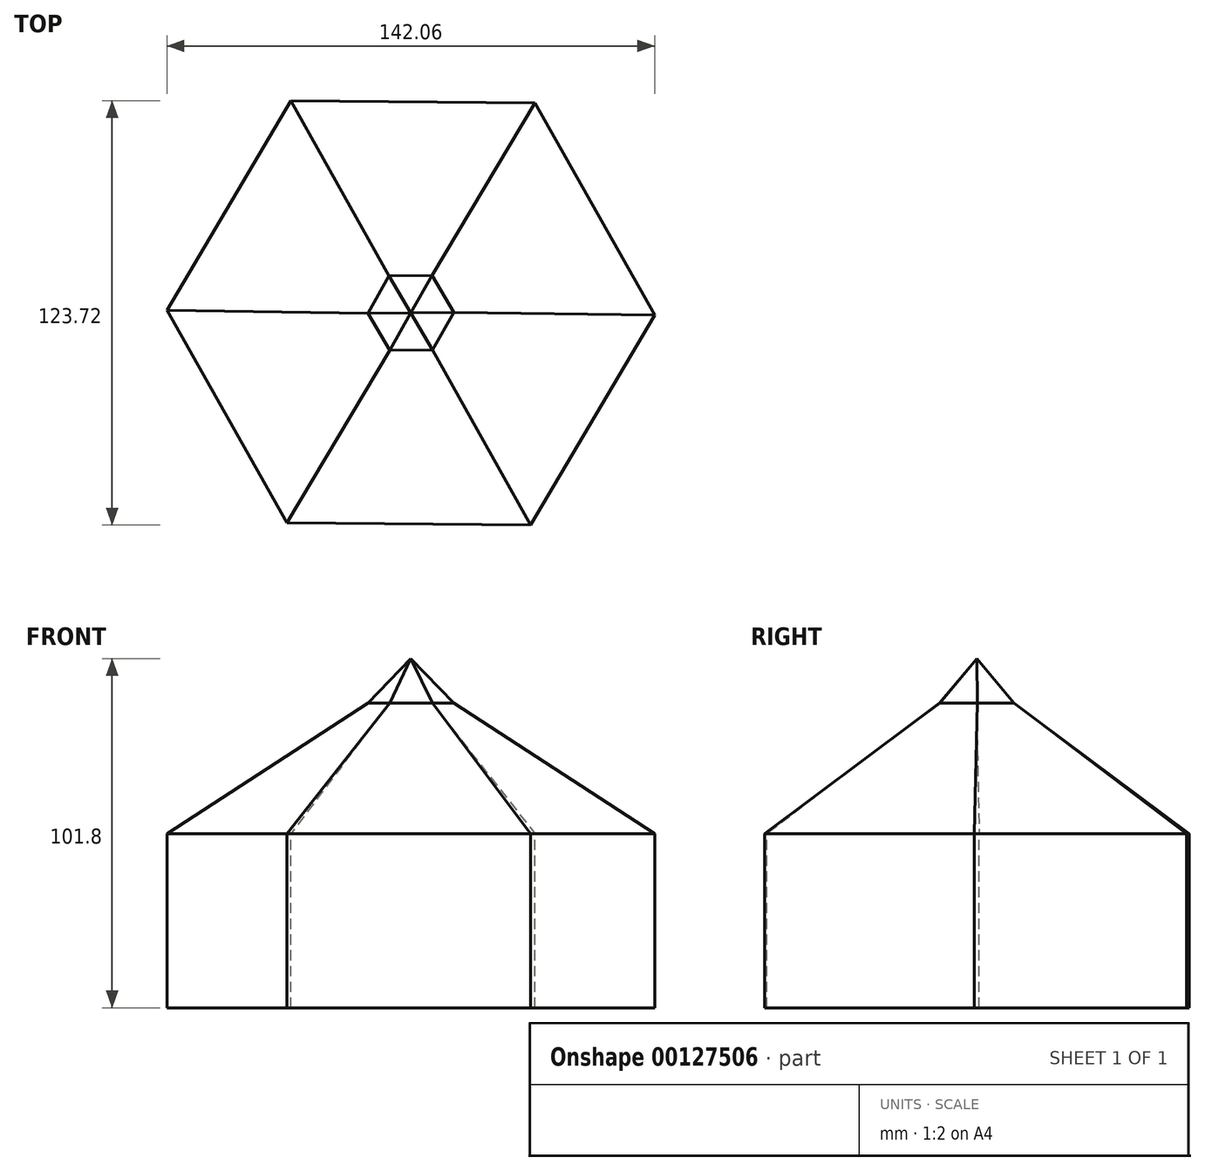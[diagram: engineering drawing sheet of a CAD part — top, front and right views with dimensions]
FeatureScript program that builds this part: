
annotation { "Feature Type Name" : "Feature", "Feature Type Description" : "" }
export const myFeature = defineFeature(function(context is Context, id is Id, definition is map)
    precondition{}
    {
        {
            var Q0;
            Q0=qCreatedBy(makeId("Top.planeOp"),FACE);
            cPlane(context, id + "F0", {"entities" : qUnion([Q0]), "cplaneType" : CPlaneType.OFFSET, "offset" : 38.1 * mm, "width" : 152.4 * mm, "height" : 152.4 * mm});
        }
        {
            var Q0;
            Q0=qCreatedBy(makeId("Top.planeOp"),FACE);
            var sketch = newSketch(context, id + "F1", { "sketchPlane" : qUnion([Q0])});
            skCircle(sketch, "E0.cCircle", {"center": v(0, 0) * mm, "radius": 61.51 * mm, "construction": true});
            skLineSegment(sketch, "E0.0", {"start": v(36.1, 61.17) * mm, "end": v(71.03, -0.69) * mm});
            skLineSegment(sketch, "E0.1", {"start": v(71.03, -0.69) * mm, "end": v(34.92, -61.86) * mm});
            skLineSegment(sketch, "E0.2", {"start": v(34.92, -61.86) * mm, "end": v(-36.1, -61.17) * mm});
            skLineSegment(sketch, "E0.3", {"start": v(-36.1, -61.17) * mm, "end": v(-71.03, 0.69) * mm});
            skLineSegment(sketch, "E0.4", {"start": v(-71.03, 0.69) * mm, "end": v(-34.92, 61.86) * mm});
            skLineSegment(sketch, "E0.5", {"start": v(-34.92, 61.86) * mm, "end": v(36.1, 61.17) * mm});
            skPoint(sketch, "E0.0.midPoint", {"position": v(53.57, 30.24) * mm});
            skSolve(sketch);
        }
        {
            var Q0;
            Q0 = qSketchRegion(id + "F1", true);
            extrude(context, id + "F2", {"entities" : qUnion([Q0]), "oppositeDirection" : true, "depth" : 50.8 * mm});
        }
        {
            var Q0;
            Q0=qCreatedBy(id+"F0.planeOp",FACE);
            var sketch = newSketch(context, id + "F3", { "sketchPlane" : qUnion([Q0])});
            skCircle(sketch, "E1.cCircle", {"center": v(0, 0) * mm, "radius": 10.83 * mm, "construction": true});
            skLineSegment(sketch, "E1.0", {"start": v(12.5, 0.11) * mm, "end": v(6.35, -10.77) * mm});
            skLineSegment(sketch, "E1.1", {"start": v(6.35, -10.77) * mm, "end": v(-6.15, -10.88) * mm});
            skLineSegment(sketch, "E1.2", {"start": v(-6.15, -10.88) * mm, "end": v(-12.5, -0.11) * mm});
            skLineSegment(sketch, "E1.3", {"start": v(-12.5, -0.11) * mm, "end": v(-6.35, 10.77) * mm});
            skLineSegment(sketch, "E1.4", {"start": v(-6.35, 10.77) * mm, "end": v(6.15, 10.88) * mm});
            skLineSegment(sketch, "E1.5", {"start": v(6.15, 10.88) * mm, "end": v(12.5, 0.11) * mm});
            skPoint(sketch, "E1.0.midPoint", {"position": v(9.42, -5.33) * mm});
            skSolve(sketch);
        }
        {
            var Q1;
            Q1=makeQuery(id+"F3.imprint","IMPRINT",FACE,{"disambiguationData":[TD([[makeQuery(id+"F3.imprint","IMPRINT",EDGE,{"derivedFrom":sQuery(id+"F3.wireOp",EDGE,"E1.0")}),-1.0]])]});
            var Q2;
            Q2=makeQuery(id+"F2.opExtrude","CAP_FACE",FACE,{"disambiguationData":[OSD([sQuery(id+"F1.wireOp",EDGE,"E0.0"),sQuery(id+"F1.wireOp",EDGE,"E0.1"),sQuery(id+"F1.wireOp",EDGE,"E0.2"),sQuery(id+"F1.wireOp",EDGE,"E0.3"),sQuery(id+"F1.wireOp",EDGE,"E0.4"),sQuery(id+"F1.wireOp",EDGE,"E0.5")])],"isStart":true});
            loft(context, id + "F4", {"operationType" : NewBodyOperationType.ADD, "sheetProfilesArray" : [{ "sheetProfileEntities" : qUnion([Q1]) }, { "sheetProfileEntities" : qUnion([Q2]) }]});
        }
        {
            var Q0;
            Q0=makeQuery(id+"F4.opLoft","CAP_FACE",FACE,{"disambiguationData":[OSD([makeQuery(id+"F3.imprint","IMPRINT",FACE,{"disambiguationData":[TD([[makeQuery(id+"F3.imprint","IMPRINT",EDGE,{"derivedFrom":sQuery(id+"F3.wireOp",EDGE,"E1.0")}),-1.0]])]})])],"isStart":true});
            extrude(context, id + "F5", {"entities" : qUnion([Q0]), "operationType" : NewBodyOperationType.ADD, "depth" : 50.8 * mm, "hasDraft" : true, "draftAngle" : 40 * degree, "draftPullDirection" : true});
        }
    });
